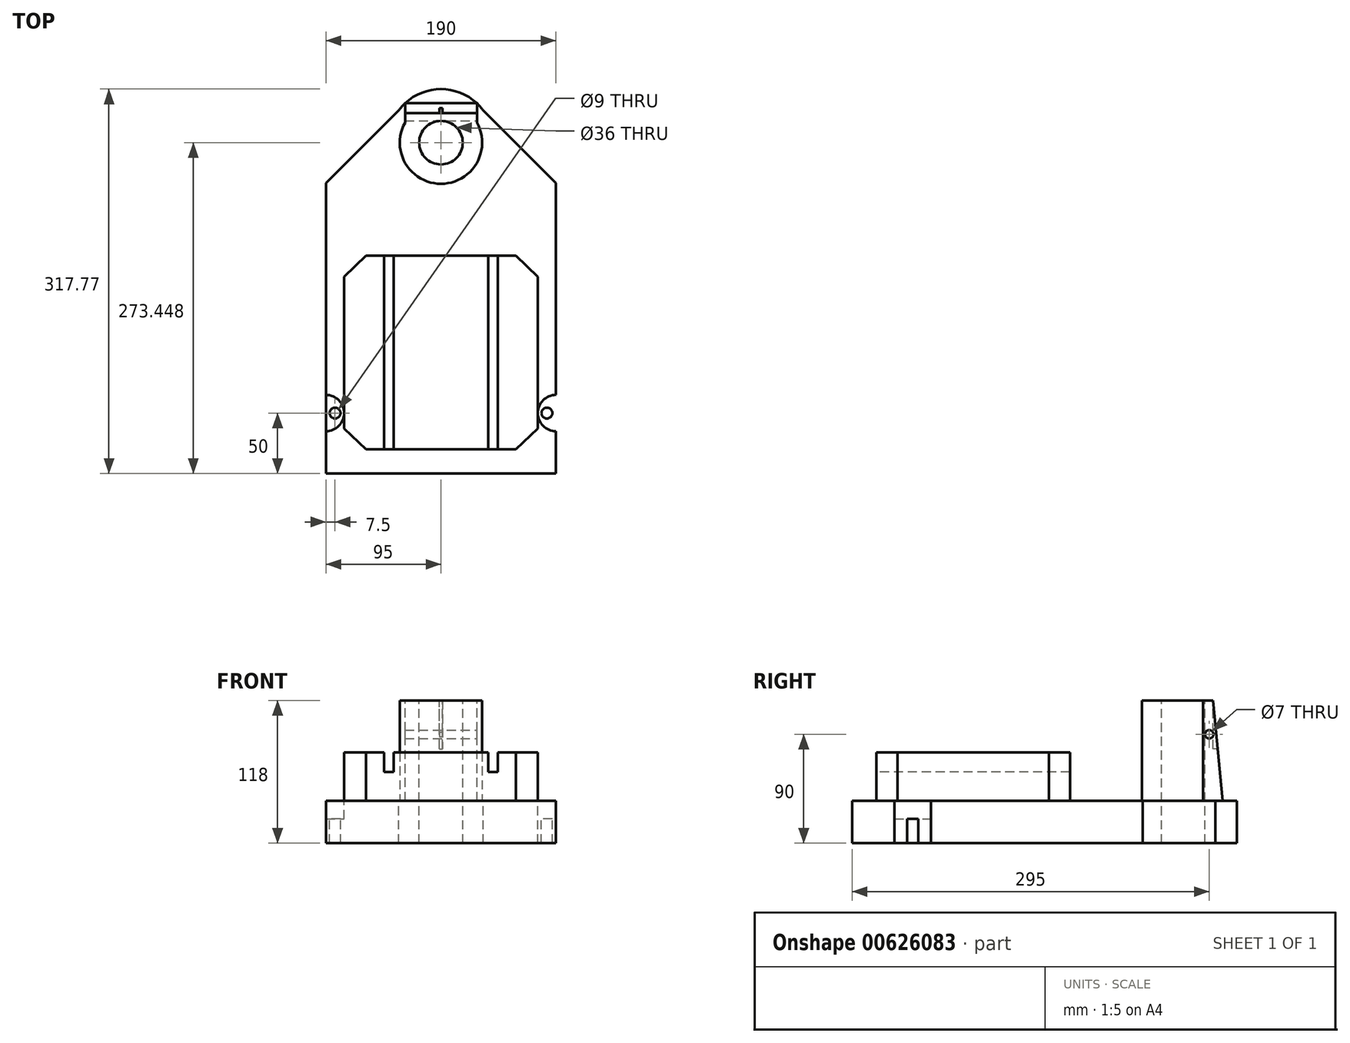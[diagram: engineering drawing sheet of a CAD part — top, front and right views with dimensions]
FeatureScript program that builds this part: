
annotation { "Feature Type Name" : "Feature", "Feature Type Description" : "" }
export const myFeature = defineFeature(function(context is Context, id is Id, definition is map)
    precondition{}
    {
        {
            var Q0;
            Q0=qCreatedBy(makeId("Top.planeOp"),FACE);
            var sketch = newSketch(context, id + "F0", { "sketchPlane" : qUnion([Q0])});
            skLineSegment(sketch, "E0", {"start": v(-35, 160) * mm, "end": v(35, 160) * mm});
            skLineSegment(sketch, "E1", {"start": v(35, 160) * mm, "end": v(95, 100) * mm});
            skLineSegment(sketch, "E2", {"start": v(95, 100) * mm, "end": v(95, -140) * mm});
            skLineSegment(sketch, "E3", {"start": v(95, -140) * mm, "end": v(-95, -140) * mm});
            skLineSegment(sketch, "E4", {"start": v(-95, -140) * mm, "end": v(-95, 100) * mm});
            skLineSegment(sketch, "E5", {"start": v(-95, 100) * mm, "end": v(-35, 160) * mm});
            skLineSegment(sketch, "E6", {"start": v(0, 205.77) * mm, "end": v(0, -202.14) * mm, "construction": true});
            skPoint(sketch, "E6.startSnap0", {"position": v(0, 160) * mm});
            skLineSegment(sketch, "E7.bottom", {"start": v(-80, 40) * mm, "end": v(80, 40) * mm});
            skLineSegment(sketch, "E7.top", {"start": v(-80, -120) * mm, "end": v(80, -120) * mm});
            skLineSegment(sketch, "E7.left", {"start": v(-80, 40) * mm, "end": v(-80, -120) * mm});
            skLineSegment(sketch, "E7.right", {"start": v(80, 40) * mm, "end": v(80, -120) * mm});
            skArc(sketch, "E8", {"start": v(-95, -105) * mm, "mid": v(-80, -90) * mm, "end": v(-95, -75) * mm});
            skCircle(sketch, "E9", {"center": v(-87.5, -90) * mm, "radius": 4.5 * mm});
            skCircle(sketch, "E10.MirrorC", {"center": v(87.5, -90) * mm, "radius": 4.5 * mm});
            skArc(sketch, "E11.MirrorCS", {"start": v(95, -105) * mm, "mid": v(80, -90) * mm, "end": v(95, -75) * mm});
            skSolve(sketch);
        }
        {
            var Q0;
            Q0=makeQuery(id+"F0.imprint","IMPRINT",FACE,{"disambiguationData":[TD([[makeQuery(id+"F0.imprint","IMPRINT",EDGE,{"derivedFrom":sQuery(id+"F0.wireOp",EDGE,"E0")}),-1.0]])]});
            var Q1;
            {var subQ3=sQuery(id+"F0.wireOp",EDGE,"E7.bottom");Q1=makeQuery(id+"F0.imprint","IMPRINT",FACE,{"disambiguationData":[TD([[makeQuery(id+"F0.imprint","IMPRINT",EDGE,{"derivedFrom":subQ3}),-1.0]])]});}
            var Q2;
            {var subQ2=sQuery(id+"F0.wireOp",EDGE,"E3");Q2=makeQuery(id+"F0.imprint","IMPRINT",FACE,{"disambiguationData":[TD([[makeQuery(id+"F0.imprint","IMPRINT",EDGE,{"derivedFrom":subQ2}),-1.0]])]});}
            var Q3;
            Q3=makeQuery(id+"F0.imprint","IMPRINT",FACE,{"disambiguationData":[TD([[makeQuery(id+"F0.imprint","IMPRINT",EDGE,{"derivedFrom":sQuery(id+"F0.wireOp",EDGE,"E10.MirrorC")}),1.0]])]});
            var Q4;
            Q4=makeQuery(id+"F0.imprint","IMPRINT",FACE,{"disambiguationData":[TD([[makeQuery(id+"F0.imprint","IMPRINT",EDGE,{"derivedFrom":sQuery(id+"F0.wireOp",EDGE,"E9")}),-1.0]])]});
            extrude(context, id + "F1", {"entities" : qUnion([Q0, Q1, Q2, Q3, Q4]), "oppositeDirection" : true, "depth" : 35 * mm, "offsetDistance" : 25 * mm});
        }
        {
            var Q0;
            {var subQ3=sQuery(id+"F0.wireOp",EDGE,"E7.bottom");Q0=makeQuery(id+"F0.imprint","IMPRINT",FACE,{"disambiguationData":[TD([[makeQuery(id+"F0.imprint","IMPRINT",EDGE,{"derivedFrom":subQ3}),-1.0]])]});}
            extrude(context, id + "F2", {"entities" : qUnion([Q0]), "operationType" : NewBodyOperationType.ADD, "depth" : 24 * mm, "offsetDistance" : 25 * mm});
        }
        {
            var Q0;
            Q0=makeQuery(id+"F0.imprint","IMPRINT",FACE,{"disambiguationData":[TD([[makeQuery(id+"F0.imprint","IMPRINT",EDGE,{"derivedFrom":sQuery(id+"F0.wireOp",EDGE,"E9")}),-1.0]])]});
            var Q1;
            Q1=makeQuery(id+"F0.imprint","IMPRINT",FACE,{"disambiguationData":[TD([[makeQuery(id+"F0.imprint","IMPRINT",EDGE,{"derivedFrom":sQuery(id+"F0.wireOp",EDGE,"E10.MirrorC")}),1.0]])]});
            extrude(context, id + "F3", {"entities" : qUnion([Q0, Q1]), "operationType" : NewBodyOperationType.REMOVE, "oppositeDirection" : true, "depth" : 15 * mm, "offsetDistance" : 25 * mm});
        }
        {
            var Q0;
            Q0=makeQuery(id+"F0.imprint","IMPRINT",FACE,{"disambiguationData":[TD([[makeQuery(id+"F0.imprint","IMPRINT",EDGE,{"derivedFrom":sQuery(id+"F0.wireOp",EDGE,"E0")}),-1.0]])]});
            var sketch = newSketch(context, id + "F4", { "sketchPlane" : qUnion([Q0])});
            skArc(sketch, "E12", {"start": v(35, 160) * mm, "mid": v(0, 177.77) * mm, "end": v(-35, 160) * mm});
            skSolve(sketch);
        }
        {
            var Q0;
            Q0=makeQuery(id+"F4.imprint","IMPRINT",FACE,{"disambiguationData":[TD([[makeQuery(id+"F4.imprint","IMPRINT",EDGE,{"derivedFrom":sQuery(id+"F4.wireOp",EDGE,"E12")}),1.0]])]});
            extrude(context, id + "F5", {"entities" : qUnion([Q0]), "operationType" : NewBodyOperationType.ADD, "oppositeDirection" : true, "depth" : 35 * mm, "offsetDistance" : 25 * mm});
        }
        {
            var Q0;
            {var subQ0=sQuery(id+"F0.wireOp",EDGE,"E0");var subQ1=sQuery(id+"F0.wireOp",EDGE,"E5");var subQ2=sQuery(id+"F0.wireOp",EDGE,"E4");var subQ3=sQuery(id+"F0.wireOp",EDGE,"E2");var subQ4=sQuery(id+"F0.wireOp",EDGE,"E1");var subQ5=makeQuery(id+"F1.opExtrude","CAP_FACE",FACE,{"disambiguationData":[OSD([subQ0,subQ4,subQ3,sQuery(id+"F0.wireOp",EDGE,"E3"),subQ2,subQ1,sQuery(id+"F0.wireOp",EDGE,"E9"),sQuery(id+"F0.wireOp",EDGE,"E10.MirrorC")])],"isStart":true});Q0=makeQuery(id+"F5.boolean.opBoolean","MERGE",FACE,{"derivedFrom":[makeQuery(id+"F3.boolean.opBoolean","SPLIT",FACE,{"disambiguationData":[TD([makeQuery(id+"F1.opExtrude","SWEPT_FACE",FACE,{"disambiguationData":[OSD([subQ0])]})])],"derivedFrom":subQ5}),makeQuery(id+"F5.opExtrude","CAP_FACE",FACE,{"disambiguationData":[OSD([subQ0,sQuery(id+"F4.wireOp",EDGE,"E12")])],"isStart":true})]});}
            var sketch = newSketch(context, id + "F6", { "sketchPlane" : qUnion([Q0])});
            skLineSegment(sketch, "E13", {"start": v(-29.7, 166) * mm, "end": v(29.7, 166) * mm});
            skLineSegment(sketch, "E14", {"start": v(29.7, 166) * mm, "end": v(29.7, 150) * mm});
            skLineSegment(sketch, "E15", {"start": v(-29.7, 166) * mm, "end": v(-29.7, 150) * mm});
            skArc(sketch, "E16.trimOffspring", {"start": v(-29.7, 150) * mm, "mid": v(0, 99.45) * mm, "end": v(29.7, 150) * mm});
            skSolve(sketch);
        }
        {
            var Q0;
            Q0=makeQuery(id+"F6.imprint","IMPRINT",FACE,{"disambiguationData":[TD([[makeQuery(id+"F6.imprint","IMPRINT",EDGE,{"derivedFrom":sQuery(id+"F6.wireOp",EDGE,"E13")}),-1.0]])]});
            extrude(context, id + "F7", {"entities" : qUnion([Q0]), "operationType" : NewBodyOperationType.ADD, "depth" : 83 * mm, "offsetDistance" : 25 * mm});
        }
        {
            var Q0;
            Q0=makeQuery(id+"F7.opExtrude","SWEPT_FACE",FACE,{"disambiguationData":[OSD([sQuery(id+"F6.wireOp",EDGE,"E14")])]});
            var sketch = newSketch(context, id + "F8", { "sketchPlane" : qUnion([Q0])});
            skLineSegment(sketch, "E17", {"start": v(166, 0) * mm, "end": v(158, 83) * mm});
            skCircle(sketch, "E18", {"center": v(155, 55) * mm, "radius": 3.5 * mm});
            skSolve(sketch);
        }
        {
            var Q0;
            {var subQ0=sQuery(id+"F8.wireOp",EDGE,"E17");Q0=makeQuery(id+"F8.imprint","IMPRINT",FACE,{"disambiguationData":[TD([[makeQuery(id+"F8.imprint","IMPRINT",EDGE,{"derivedFrom":subQ0}),-1.0]])]});}
            extrude(context, id + "F9", {"entities" : qUnion([Q0]), "operationType" : NewBodyOperationType.REMOVE, "oppositeDirection" : true, "depth" : 125 * mm, "offsetDistance" : 25 * mm});
        }
        {
            var Q0;
            Q0=makeQuery(id+"F7.opExtrude","CAP_FACE",FACE,{"disambiguationData":[OSD([sQuery(id+"F6.wireOp",EDGE,"E13"),sQuery(id+"F6.wireOp",EDGE,"E14"),sQuery(id+"F6.wireOp",EDGE,"E15"),sQuery(id+"F6.wireOp",EDGE,"E16.trimOffspring")])],"isStart":false});
            var sketch = newSketch(context, id + "F10", { "sketchPlane" : qUnion([Q0])});
            skCircle(sketch, "E19", {"center": v(0, 133.45) * mm, "radius": 18 * mm});
            skSolve(sketch);
        }
        {
            var Q0;
            Q0=makeQuery(id+"F10.imprint","IMPRINT",FACE,{"disambiguationData":[TD([[makeQuery(id+"F10.imprint","IMPRINT",EDGE,{"derivedFrom":sQuery(id+"F10.wireOp",EDGE,"E19")}),1.0]])]});
            extrude(context, id + "F11", {"entities" : qUnion([Q0]), "operationType" : NewBodyOperationType.REMOVE, "oppositeDirection" : true, "depth" : 222 * mm, "offsetDistance" : 25 * mm});
        }
        {
            var Q0;
            Q0=makeQuery(id+"F7.opExtrude","CAP_FACE",FACE,{"disambiguationData":[OSD([sQuery(id+"F6.wireOp",EDGE,"E13"),sQuery(id+"F6.wireOp",EDGE,"E14"),sQuery(id+"F6.wireOp",EDGE,"E15"),sQuery(id+"F6.wireOp",EDGE,"E16.trimOffspring")])],"isStart":false});
            var sketch = newSketch(context, id + "F12", { "sketchPlane" : qUnion([Q0])});
            skLineSegment(sketch, "E20", {"start": v(-1.25, 190) * mm, "end": v(-1.25, 140) * mm});
            skLineSegment(sketch, "E21", {"start": v(-1.25, 140) * mm, "end": v(1.25, 140) * mm});
            skLineSegment(sketch, "E22", {"start": v(1.25, 140) * mm, "end": v(1.25, 190) * mm});
            skLineSegment(sketch, "E23", {"start": v(1.25, 190) * mm, "end": v(-1.25, 190) * mm});
            skPoint(sketch, "E24.positionSnap0", {"position": v(0, 140) * mm});
            skSolve(sketch);
        }
        {
            var Q0;
            {var subQ0=sQuery(id+"F12.wireOp",EDGE,"E23");Q0=makeQuery(id+"F12.imprint","IMPRINT",FACE,{"disambiguationData":[TD([[makeQuery(id+"F12.imprint","IMPRINT",EDGE,{"derivedFrom":subQ0}),1.0]])]});}
            var Q1;
            {var subQ0=sQuery(id+"F12.wireOp",EDGE,"E20");var subQ3=makeQuery(id+"F11.boolean.opBoolean","COPY",EDGE,{"derivedFrom":makeQuery(id+"F11.opExtrude","CAP_EDGE",EDGE,{"disambiguationData":[OSD([sQuery(id+"F10.wireOp",EDGE,"E19")])],"isStart":true})});var subQ4=makeQuery(id+"F12.imprint","INTERSECT",VERTEX,{"derivedFrom":[subQ3,subQ0]});Q1=makeQuery(id+"F12.imprint","IMPRINT",FACE,{"disambiguationData":[TD([[makeQuery(id+"F12.imprint","IMPRINT",EDGE,{"disambiguationData":[TD([[subQ4,1.0]])],"derivedFrom":subQ3}),-1.0]])]});}
            var Q2;
            {var subQ0=sQuery(id+"F12.wireOp",EDGE,"E21");Q2=makeQuery(id+"F12.imprint","IMPRINT",FACE,{"disambiguationData":[TD([[makeQuery(id+"F12.imprint","IMPRINT",EDGE,{"derivedFrom":subQ0}),1.0]])]});}
            extrude(context, id + "F13", {"entities" : qUnion([Q0, Q1, Q2]), "operationType" : NewBodyOperationType.REMOVE, "oppositeDirection" : true, "depth" : 40 * mm, "offsetDistance" : 25 * mm});
        }
        {
            var Q0;
            Q0=makeQuery(id+"F8.imprint","IMPRINT",FACE,{"disambiguationData":[TD([[makeQuery(id+"F8.imprint","IMPRINT",EDGE,{"derivedFrom":sQuery(id+"F8.wireOp",EDGE,"E18")}),1.0]])]});
            extrude(context, id + "F14", {"entities" : qUnion([Q0]), "operationType" : NewBodyOperationType.REMOVE, "oppositeDirection" : true, "depth" : 94.3 * mm, "offsetDistance" : 25 * mm});
        }
        {
            var Q0;
            Q0=makeQuery(id+"F2.opExtrude","CAP_FACE",FACE,{"disambiguationData":[OSD([sQuery(id+"F0.wireOp",EDGE,"E7.bottom"),sQuery(id+"F0.wireOp",EDGE,"E7.top"),sQuery(id+"F0.wireOp",EDGE,"E7.left"),sQuery(id+"F0.wireOp",EDGE,"E7.right")])],"isStart":false});
            var sketch = newSketch(context, id + "F15", { "sketchPlane" : qUnion([Q0])});
            skLineSegment(sketch, "E25", {"start": v(-47, 40) * mm, "end": v(-47, -120) * mm});
            skLineSegment(sketch, "E26", {"start": v(-39, 40) * mm, "end": v(-39, -120) * mm});
            skLineSegment(sketch, "E27", {"start": v(-62, 40) * mm, "end": v(-80, 22.65) * mm});
            skLineSegment(sketch, "E28", {"start": v(-62, -120) * mm, "end": v(-80, -102.65) * mm});
            skLineSegment(sketch, "E29.MirrorCS", {"start": v(39, 40) * mm, "end": v(39, -120) * mm});
            skLineSegment(sketch, "E30.MirrorCS", {"start": v(47, 40) * mm, "end": v(47, -120) * mm});
            skLineSegment(sketch, "E31.MirrorCS", {"start": v(62, 40) * mm, "end": v(80, 22.65) * mm});
            skLineSegment(sketch, "E32.MirrorCS", {"start": v(62, -120) * mm, "end": v(80, -102.65) * mm});
            skSolve(sketch);
        }
        {
            var Q0;
            {var subQ0=sQuery(id+"F15.wireOp",EDGE,"E30.MirrorCS");Q0=makeQuery(id+"F15.imprint","IMPRINT",FACE,{"disambiguationData":[TD([[makeQuery(id+"F15.imprint","IMPRINT",EDGE,{"derivedFrom":subQ0}),1.0]])]});}
            var Q1;
            {var subQ0=sQuery(id+"F15.wireOp",EDGE,"E26");Q1=makeQuery(id+"F15.imprint","IMPRINT",FACE,{"disambiguationData":[TD([[makeQuery(id+"F15.imprint","IMPRINT",EDGE,{"derivedFrom":subQ0}),1.0]])]});}
            var Q2;
            {var subQ0=sQuery(id+"F15.wireOp",EDGE,"E25");Q2=makeQuery(id+"F15.imprint","IMPRINT",FACE,{"disambiguationData":[TD([[makeQuery(id+"F15.imprint","IMPRINT",EDGE,{"derivedFrom":subQ0}),-1.0]])]});}
            extrude(context, id + "F16", {"entities" : qUnion([Q0, Q1, Q2]), "operationType" : NewBodyOperationType.ADD, "depth" : 16 * mm, "offsetDistance" : 25 * mm});
        }
        {
            var Q0;
            {var subQ0=sQuery(id+"F0.wireOp",EDGE,"E7.bottom");var subQ2=sQuery(id+"F15.wireOp",EDGE,"E27");var subQ3=sQuery(id+"F0.wireOp",EDGE,"E7.left");Q0=makeQuery(id+"F16.boolean.opBoolean","SPLIT",FACE,{"disambiguationData":[TD([makeQuery(id+"F16.opExtrude","SWEPT_FACE",FACE,{"disambiguationData":[OSD([subQ2])]})])],"derivedFrom":makeQuery(id+"F2.opExtrude","CAP_FACE",FACE,{"disambiguationData":[OSD([subQ0,sQuery(id+"F0.wireOp",EDGE,"E7.top"),subQ3,sQuery(id+"F0.wireOp",EDGE,"E7.right")])],"isStart":false})});}
            var Q1;
            {var subQ0=sQuery(id+"F0.wireOp",EDGE,"E7.top");var subQ2=sQuery(id+"F15.wireOp",EDGE,"E28");var subQ3=sQuery(id+"F0.wireOp",EDGE,"E7.left");Q1=makeQuery(id+"F16.boolean.opBoolean","SPLIT",FACE,{"disambiguationData":[TD([makeQuery(id+"F16.opExtrude","SWEPT_FACE",FACE,{"disambiguationData":[OSD([subQ2])]})])],"derivedFrom":makeQuery(id+"F2.opExtrude","CAP_FACE",FACE,{"disambiguationData":[OSD([sQuery(id+"F0.wireOp",EDGE,"E7.bottom"),subQ0,subQ3,sQuery(id+"F0.wireOp",EDGE,"E7.right")])],"isStart":false})});}
            var Q2;
            {var subQ0=sQuery(id+"F0.wireOp",EDGE,"E7.top");var subQ2=sQuery(id+"F15.wireOp",EDGE,"E32.MirrorCS");var subQ3=sQuery(id+"F0.wireOp",EDGE,"E7.right");Q2=makeQuery(id+"F16.boolean.opBoolean","SPLIT",FACE,{"disambiguationData":[TD([makeQuery(id+"F16.opExtrude","SWEPT_FACE",FACE,{"disambiguationData":[OSD([subQ2])]})])],"derivedFrom":makeQuery(id+"F2.opExtrude","CAP_FACE",FACE,{"disambiguationData":[OSD([sQuery(id+"F0.wireOp",EDGE,"E7.bottom"),subQ0,sQuery(id+"F0.wireOp",EDGE,"E7.left"),subQ3])],"isStart":false})});}
            var Q3;
            {var subQ0=sQuery(id+"F0.wireOp",EDGE,"E7.bottom");var subQ2=sQuery(id+"F15.wireOp",EDGE,"E31.MirrorCS");var subQ3=sQuery(id+"F0.wireOp",EDGE,"E7.right");Q3=makeQuery(id+"F16.boolean.opBoolean","SPLIT",FACE,{"disambiguationData":[TD([makeQuery(id+"F16.opExtrude","SWEPT_FACE",FACE,{"disambiguationData":[OSD([subQ2])]})])],"derivedFrom":makeQuery(id+"F2.opExtrude","CAP_FACE",FACE,{"disambiguationData":[OSD([subQ0,sQuery(id+"F0.wireOp",EDGE,"E7.top"),sQuery(id+"F0.wireOp",EDGE,"E7.left"),subQ3])],"isStart":false})});}
            extrude(context, id + "F17", {"entities" : qUnion([Q0, Q1, Q2, Q3]), "operationType" : NewBodyOperationType.REMOVE, "oppositeDirection" : true, "depth" : 24 * mm, "offsetDistance" : 25 * mm});
        }
    });
